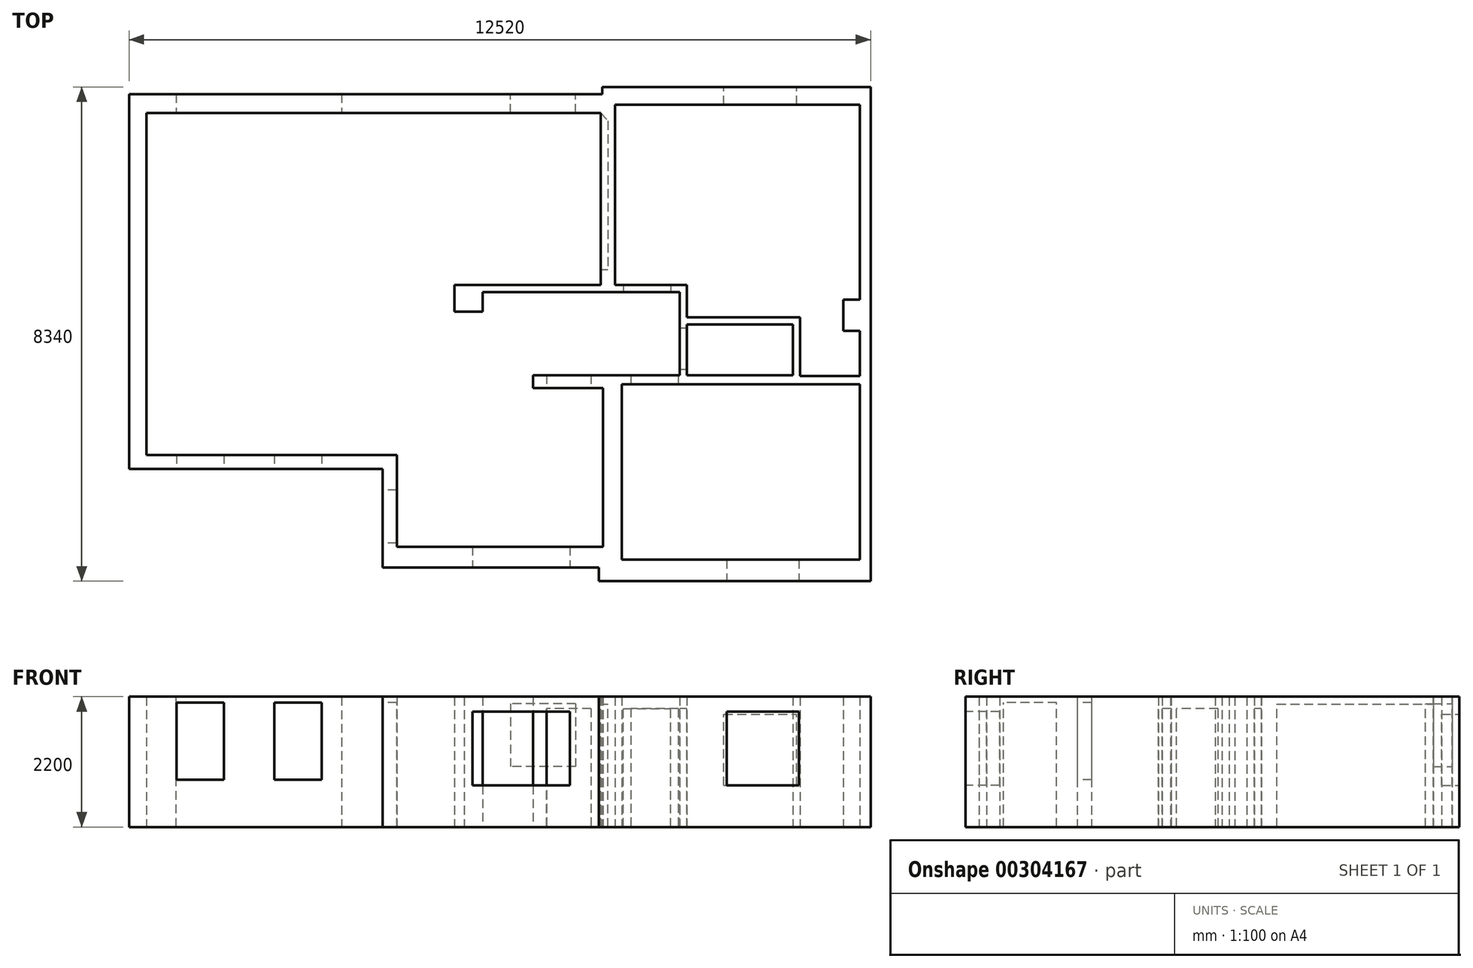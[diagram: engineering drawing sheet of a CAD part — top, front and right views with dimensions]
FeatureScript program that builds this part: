
annotation { "Feature Type Name" : "Feature", "Feature Type Description" : "" }
export const myFeature = defineFeature(function(context is Context, id is Id, definition is map)
    precondition{}
    {
        {
            var Q0;
            Q0=qCreatedBy(makeId("Top.planeOp"),FACE);
            var sketch = newSketch(context, id + "F0", { "sketchPlane" : qUnion([Q0])});
            skLineSegment(sketch, "E0", {"start": v(890, -1585.96) * mm, "end": v(-3390, -1585.96) * mm});
            skLineSegment(sketch, "E1", {"start": v(-3390, 4744.04) * mm, "end": v(-3390, -1585.96) * mm});
            skLineSegment(sketch, "E2", {"start": v(890, -3245.96) * mm, "end": v(4540, -3245.96) * mm});
            skLineSegment(sketch, "E3", {"start": v(4610, -2895.96) * mm, "end": v(1130, -2895.96) * mm});
            skLineSegment(sketch, "E4", {"start": v(4540, -3245.96) * mm, "end": v(4540, -3475.96) * mm});
            skLineSegment(sketch, "E5", {"start": v(4540, -3475.96) * mm, "end": v(9130, -3475.96) * mm});
            skLineSegment(sketch, "E6", {"start": v(9130, -3475.96) * mm, "end": v(9130, 4864.04) * mm});
            skLineSegment(sketch, "E7", {"start": v(9130, 4864.04) * mm, "end": v(4600, 4864.04) * mm});
            skLineSegment(sketch, "E8", {"start": v(4815, 4564.04) * mm, "end": v(8950, 4564.04) * mm});
            skLineSegment(sketch, "E9", {"start": v(8950, -3115.96) * mm, "end": v(4930, -3115.96) * mm});
            skLineSegment(sketch, "E10", {"start": v(8950, -155.96) * mm, "end": v(4930, -155.96) * mm});
            skLineSegment(sketch, "E11.bottom", {"start": v(8950, 1274.04) * mm, "end": v(8670, 1274.04) * mm});
            skLineSegment(sketch, "E11.top", {"start": v(8950, 744.04) * mm, "end": v(8670, 744.04) * mm});
            skLineSegment(sketch, "E11.right", {"start": v(8670, 1274.04) * mm, "end": v(8670, 744.04) * mm});
            skLineSegment(sketch, "E12", {"start": v(2020, 4424.04) * mm, "end": v(2020, 1518.96) * mm});
            skLineSegment(sketch, "E13", {"start": v(2020, 1518.96) * mm, "end": v(1110, 1518.96) * mm});
            skLineSegment(sketch, "E14", {"start": v(5905, 1400) * mm, "end": v(5905, 0) * mm});
            skLineSegment(sketch, "E15", {"start": v(7935, -15.96) * mm, "end": v(7935, 974.04) * mm});
            skLineSegment(sketch, "E16", {"start": v(7935, 974.04) * mm, "end": v(6025, 974.04) * mm});
            skLineSegment(sketch, "E17", {"start": v(6025, 974.04) * mm, "end": v(6025, 1524.04) * mm});
            skLineSegment(sketch, "E18", {"start": v(6025, 1524.04) * mm, "end": v(4815, 1524.04) * mm});
            skLineSegment(sketch, "E19", {"start": v(4815, 1524.04) * mm, "end": v(4815, 4564.04) * mm});
            skLineSegment(sketch, "E20", {"start": v(4695, 1524.04) * mm, "end": v(2215, 1524.04) * mm});
            skLineSegment(sketch, "E21", {"start": v(2215, 1524.04) * mm, "end": v(2215, 4424.04) * mm});
            skLineSegment(sketch, "E22", {"start": v(2100, 1400) * mm, "end": v(2100, 1070) * mm});
            skLineSegment(sketch, "E23", {"start": v(2100, 1070) * mm, "end": v(2580, 1070) * mm});
            skLineSegment(sketch, "E24", {"start": v(2580, 1070) * mm, "end": v(2580, 1400) * mm});
            skLineSegment(sketch, "E25", {"start": v(4695, 4424.04) * mm, "end": v(4695, 1524.04) * mm});
            skLineSegment(sketch, "E26", {"start": v(4695, 4424.04) * mm, "end": v(2215, 4424.04) * mm});
            skLineSegment(sketch, "E27", {"start": v(2020, 4424.04) * mm, "end": v(-3100, 4424.04) * mm});
            skLineSegment(sketch, "E28", {"start": v(-3100, 4424.04) * mm, "end": v(-3100, -1345.96) * mm});
            skLineSegment(sketch, "E29", {"start": v(890, -1585.96) * mm, "end": v(890, -3245.96) * mm});
            skLineSegment(sketch, "E30", {"start": v(4610, -215.96) * mm, "end": v(4610, -2895.96) * mm});
            skLineSegment(sketch, "E31", {"start": v(4930, -155.96) * mm, "end": v(4930, -3115.96) * mm});
            skLineSegment(sketch, "E32", {"start": v(8950, -155.96) * mm, "end": v(8950, -3115.96) * mm});
            skLineSegment(sketch, "E33", {"start": v(8950, -15.96) * mm, "end": v(8950, 744.04) * mm});
            skLineSegment(sketch, "E34", {"start": v(8950, 1274.04) * mm, "end": v(8950, 4564.04) * mm});
            skLineSegment(sketch, "E35", {"start": v(7935, -15.96) * mm, "end": v(8950, -15.96) * mm});
            skLineSegment(sketch, "E36", {"start": v(1110, 1400) * mm, "end": v(2100, 1400) * mm});
            skLineSegment(sketch, "E37", {"start": v(2580, 1400) * mm, "end": v(5905, 1400) * mm});
            skLineSegment(sketch, "E38", {"start": v(4610, -215.96) * mm, "end": v(3430, -215.96) * mm});
            skLineSegment(sketch, "E39", {"start": v(1130, -1345.96) * mm, "end": v(1130, -2895.96) * mm});
            skLineSegment(sketch, "E40", {"start": v(4600, 4864.04) * mm, "end": v(4600, 4744.04) * mm});
            skLineSegment(sketch, "E41", {"start": v(4600, 4744.04) * mm, "end": v(-3390, 4744.04) * mm});
            skLineSegment(sketch, "E42", {"start": v(-3100, -1345.96) * mm, "end": v(1130, -1345.96) * mm});
            skLineSegment(sketch, "E43", {"start": v(1110, 1400) * mm, "end": v(1110, 1518.96) * mm});
            skLineSegment(sketch, "E44", {"start": v(3430, -215.96) * mm, "end": v(3430, 0) * mm});
            skLineSegment(sketch, "E45", {"start": v(3430, 0) * mm, "end": v(5905, 0) * mm});
            skLineSegment(sketch, "E46.bottom", {"start": v(7815, 854.04) * mm, "end": v(6025, 854.04) * mm});
            skLineSegment(sketch, "E46.top", {"start": v(7815, 0) * mm, "end": v(6025, 0) * mm});
            skLineSegment(sketch, "E46.left", {"start": v(7815, 854.04) * mm, "end": v(7815, 0) * mm});
            skLineSegment(sketch, "E46.right", {"start": v(6025, 854.04) * mm, "end": v(6025, 0) * mm});
            skSolve(sketch);
        }
        {
            var Q0;
            Q0=makeQuery(id+"F0.imprint","IMPRINT",FACE,{"disambiguationData":[TD([[makeQuery(id+"F0.imprint","IMPRINT",EDGE,{"derivedFrom":sQuery(id+"F0.wireOp",EDGE,"E0")}),-1.0]])]});
            extrude(context, id + "F1", {"entities" : qUnion([Q0]), "depth" : 2200 * mm, "offsetDistance" : 25 * mm});
        }
        {
            var Q0;
            Q0=makeQuery(id+"F1.opExtrude","SWEPT_FACE",FACE,{"disambiguationData":[OSD([sQuery(id+"F0.wireOp",EDGE,"E27")])]});
            var sketch = newSketch(context, id + "F2", { "sketchPlane" : qUnion([Q0])});
            skLineSegment(sketch, "E47", {"start": v(-2600, 0) * mm, "end": v(-2600, 2199) * mm});
            skLineSegment(sketch, "E48", {"start": v(-2600, 2199) * mm, "end": v(200, 2199) * mm});
            skLineSegment(sketch, "E49", {"start": v(200, 2199) * mm, "end": v(200, 0) * mm});
            skLineSegment(sketch, "E50", {"start": v(200, 0) * mm, "end": v(-2600, 0) * mm});
            skSolve(sketch);
        }
        {
            var Q0;
            Q0 = qSketchRegion(id + "F2", true);
            extrude(context, id + "F3", {"entities" : qUnion([Q0]), "operationType" : NewBodyOperationType.REMOVE, "oppositeDirection" : true, "depth" : 350 * mm});
        }
        {
            var Q0;
            Q0=makeQuery(id+"F1.opExtrude","SWEPT_FACE",FACE,{"disambiguationData":[OSD([sQuery(id+"F0.wireOp",EDGE,"E12")])]});
            var sketch = newSketch(context, id + "F4", { "sketchPlane" : qUnion([Q0])});
            skLineSegment(sketch, "E51", {"start": v(-4424.04, 0) * mm, "end": v(-4424.04, 2200) * mm});
            skLineSegment(sketch, "E52", {"start": v(-4424.04, 2200) * mm, "end": v(-1518.96, 2200) * mm});
            skLineSegment(sketch, "E53", {"start": v(-1518.96, 2200) * mm, "end": v(-1518.96, 0) * mm});
            skLineSegment(sketch, "E54", {"start": v(-1518.96, 0) * mm, "end": v(-4424.04, 0) * mm});
            skSolve(sketch);
        }
        {
            var Q0;
            Q0 = qSketchRegion(id + "F4", true);
            extrude(context, id + "F5", {"entities" : qUnion([Q0]), "operationType" : NewBodyOperationType.REMOVE, "oppositeDirection" : true, "depth" : 250 * mm});
        }
        {
            var Q0;
            Q0=makeQuery(id+"F1.opExtrude","SWEPT_FACE",FACE,{"disambiguationData":[OSD([sQuery(id+"F0.wireOp",EDGE,"E36")])]});
            var sketch = newSketch(context, id + "F6", { "sketchPlane" : qUnion([Q0])});
            skLineSegment(sketch, "E55.bottom", {"start": v(1110, 0) * mm, "end": v(2100, 0) * mm});
            skLineSegment(sketch, "E55.top", {"start": v(1110, 2200) * mm, "end": v(2100, 2200) * mm});
            skLineSegment(sketch, "E55.left", {"start": v(1110, 0) * mm, "end": v(1110, 2200) * mm});
            skLineSegment(sketch, "E55.right", {"start": v(2100, 0) * mm, "end": v(2100, 2200) * mm});
            skSolve(sketch);
        }
        {
            var Q0;
            Q0 = qSketchRegion(id + "F6", true);
            extrude(context, id + "F7", {"entities" : qUnion([Q0]), "operationType" : NewBodyOperationType.REMOVE, "oppositeDirection" : true, "depth" : 130 * mm});
        }
        {
            var Q0;
            Q0=makeQuery(id+"F1.opExtrude","SWEPT_FACE",FACE,{"disambiguationData":[OSD([sQuery(id+"F0.wireOp",EDGE,"E38")])]});
            var sketch = newSketch(context, id + "F8", { "sketchPlane" : qUnion([Q0])});
            skLineSegment(sketch, "E56.bottom", {"start": v(3660, 0) * mm, "end": v(4410, 0) * mm});
            skLineSegment(sketch, "E56.top", {"start": v(3660, 2000) * mm, "end": v(4410, 2000) * mm});
            skLineSegment(sketch, "E56.left", {"start": v(3660, 0) * mm, "end": v(3660, 2000) * mm});
            skLineSegment(sketch, "E56.right", {"start": v(4410, 0) * mm, "end": v(4410, 2000) * mm});
            skSolve(sketch);
        }
        {
            var Q0;
            Q0 = qSketchRegion(id + "F8", true);
            extrude(context, id + "F9", {"entities" : qUnion([Q0]), "operationType" : NewBodyOperationType.REMOVE, "oppositeDirection" : true, "depth" : 250 * mm});
        }
        {
            var Q0;
            Q0=makeQuery(id+"F1.opExtrude","SWEPT_FACE",FACE,{"disambiguationData":[OSD([sQuery(id+"F0.wireOp",EDGE,"E37")])]});
            var sketch = newSketch(context, id + "F10", { "sketchPlane" : qUnion([Q0])});
            skLineSegment(sketch, "E57.bottom", {"start": v(4955, 0) * mm, "end": v(5755, 0) * mm});
            skLineSegment(sketch, "E57.top", {"start": v(4955, 2000) * mm, "end": v(5755, 2000) * mm});
            skLineSegment(sketch, "E57.left", {"start": v(4955, 0) * mm, "end": v(4955, 2000) * mm});
            skLineSegment(sketch, "E57.right", {"start": v(5755, 0) * mm, "end": v(5755, 2000) * mm});
            skSolve(sketch);
        }
        {
            var Q0;
            Q0 = qSketchRegion(id + "F10", true);
            extrude(context, id + "F11", {"entities" : qUnion([Q0]), "operationType" : NewBodyOperationType.REMOVE, "oppositeDirection" : true, "depth" : 200 * mm});
        }
        {
            var Q0;
            Q0=makeQuery(id+"F1.opExtrude","SWEPT_FACE",FACE,{"disambiguationData":[OSD([sQuery(id+"F0.wireOp",EDGE,"E10")])]});
            var sketch = newSketch(context, id + "F12", { "sketchPlane" : qUnion([Q0])});
            skLineSegment(sketch, "E58.bottom", {"start": v(5080, 0) * mm, "end": v(5880, 0) * mm});
            skLineSegment(sketch, "E58.top", {"start": v(5080, 2000) * mm, "end": v(5880, 2000) * mm});
            skLineSegment(sketch, "E58.left", {"start": v(5080, 0) * mm, "end": v(5080, 2000) * mm});
            skLineSegment(sketch, "E58.right", {"start": v(5880, 0) * mm, "end": v(5880, 2000) * mm});
            skSolve(sketch);
        }
        {
            var Q0;
            Q0 = qSketchRegion(id + "F12", true);
            extrude(context, id + "F13", {"entities" : qUnion([Q0]), "operationType" : NewBodyOperationType.REMOVE, "oppositeDirection" : true, "depth" : 200 * mm});
        }
        {
            var Q0;
            Q0=makeQuery(id+"F1.opExtrude","SWEPT_FACE",FACE,{"disambiguationData":[OSD([sQuery(id+"F0.wireOp",EDGE,"E0")])]});
            var sketch = newSketch(context, id + "F14", { "sketchPlane" : qUnion([Q0])});
            skLineSegment(sketch, "E59.bottom", {"start": v(-2590, 2100) * mm, "end": v(-1790, 2100) * mm});
            skLineSegment(sketch, "E59.top", {"start": v(-2590, 800) * mm, "end": v(-1790, 800) * mm});
            skLineSegment(sketch, "E59.left", {"start": v(-2590, 2100) * mm, "end": v(-2590, 800) * mm});
            skLineSegment(sketch, "E59.right", {"start": v(-1790, 2100) * mm, "end": v(-1790, 800) * mm});
            skLineSegment(sketch, "E60.bottom", {"start": v(-940, 2100) * mm, "end": v(-140, 2100) * mm});
            skLineSegment(sketch, "E60.top", {"start": v(-940, 800) * mm, "end": v(-140, 800) * mm});
            skLineSegment(sketch, "E60.left", {"start": v(-940, 2100) * mm, "end": v(-940, 800) * mm});
            skLineSegment(sketch, "E60.right", {"start": v(-140, 2100) * mm, "end": v(-140, 800) * mm});
            skSolve(sketch);
        }
        {
            var Q0;
            Q0 = qSketchRegion(id + "F14", true);
            extrude(context, id + "F15", {"entities" : qUnion([Q0]), "operationType" : NewBodyOperationType.REMOVE, "endBound" : BoundingType.UP_TO_NEXT, "oppositeDirection" : true, "depth" : 350 * mm});
        }
        {
            var Q0;
            Q0=makeQuery(id+"F1.opExtrude","SWEPT_FACE",FACE,{"disambiguationData":[OSD([sQuery(id+"F0.wireOp",EDGE,"E2")])]});
            var sketch = newSketch(context, id + "F16", { "sketchPlane" : qUnion([Q0])});
            skLineSegment(sketch, "E61.bottom", {"start": v(2410, 1950) * mm, "end": v(4050, 1950) * mm});
            skLineSegment(sketch, "E61.top", {"start": v(2410, 700) * mm, "end": v(4050, 700) * mm});
            skLineSegment(sketch, "E61.left", {"start": v(2410, 1950) * mm, "end": v(2410, 700) * mm});
            skLineSegment(sketch, "E61.right", {"start": v(4050, 1950) * mm, "end": v(4050, 700) * mm});
            skSolve(sketch);
        }
        {
            var Q0;
            Q0 = qSketchRegion(id + "F16", true);
            extrude(context, id + "F17", {"entities" : qUnion([Q0]), "operationType" : NewBodyOperationType.REMOVE, "endBound" : BoundingType.UP_TO_NEXT, "oppositeDirection" : true, "depth" : 25 * mm});
        }
        {
            var Q0;
            Q0=makeQuery(id+"F1.opExtrude","SWEPT_FACE",FACE,{"disambiguationData":[OSD([sQuery(id+"F0.wireOp",EDGE,"E5")])]});
            var sketch = newSketch(context, id + "F18", { "sketchPlane" : qUnion([Q0])});
            skLineSegment(sketch, "E62.bottom", {"start": v(6700, 1950) * mm, "end": v(7920, 1950) * mm});
            skLineSegment(sketch, "E62.top", {"start": v(6700, 700) * mm, "end": v(7920, 700) * mm});
            skLineSegment(sketch, "E62.left", {"start": v(6700, 1950) * mm, "end": v(6700, 700) * mm});
            skLineSegment(sketch, "E62.right", {"start": v(7920, 1950) * mm, "end": v(7920, 700) * mm});
            skSolve(sketch);
        }
        {
            var Q0;
            Q0 = qSketchRegion(id + "F18", true);
            extrude(context, id + "F19", {"entities" : qUnion([Q0]), "operationType" : NewBodyOperationType.REMOVE, "endBound" : BoundingType.UP_TO_NEXT, "oppositeDirection" : true, "depth" : 25 * mm});
        }
        {
            var Q0;
            Q0=makeQuery(id+"F1.opExtrude","SWEPT_FACE",FACE,{"disambiguationData":[OSD([sQuery(id+"F0.wireOp",EDGE,"E7")])]});
            var sketch = newSketch(context, id + "F20", { "sketchPlane" : qUnion([Q0])});
            skLineSegment(sketch, "E63.bottom", {"start": v(-7880, 1900) * mm, "end": v(-6650, 1900) * mm});
            skLineSegment(sketch, "E63.top", {"start": v(-7880, 700) * mm, "end": v(-6650, 700) * mm});
            skLineSegment(sketch, "E63.left", {"start": v(-7880, 1900) * mm, "end": v(-7880, 700) * mm});
            skLineSegment(sketch, "E63.right", {"start": v(-6650, 1900) * mm, "end": v(-6650, 700) * mm});
            skSolve(sketch);
        }
        {
            var Q0;
            Q0 = qSketchRegion(id + "F20", true);
            extrude(context, id + "F21", {"entities" : qUnion([Q0]), "operationType" : NewBodyOperationType.REMOVE, "endBound" : BoundingType.UP_TO_NEXT, "oppositeDirection" : true, "depth" : 25 * mm});
        }
        {
            var Q0;
            Q0=makeQuery(id+"F1.opExtrude","SWEPT_FACE",FACE,{"disambiguationData":[OSD([sQuery(id+"F0.wireOp",EDGE,"E41")])]});
            var sketch = newSketch(context, id + "F22", { "sketchPlane" : qUnion([Q0])});
            skLineSegment(sketch, "E64.bottom", {"start": v(-4150, 2080) * mm, "end": v(-3050, 2080) * mm});
            skLineSegment(sketch, "E64.top", {"start": v(-4150, 1020) * mm, "end": v(-3050, 1020) * mm});
            skLineSegment(sketch, "E64.left", {"start": v(-4150, 2080) * mm, "end": v(-4150, 1020) * mm});
            skLineSegment(sketch, "E64.right", {"start": v(-3050, 2080) * mm, "end": v(-3050, 1020) * mm});
            skSolve(sketch);
        }
        {
            var Q0;
            Q0 = qSketchRegion(id + "F22", true);
            extrude(context, id + "F23", {"entities" : qUnion([Q0]), "operationType" : NewBodyOperationType.REMOVE, "endBound" : BoundingType.UP_TO_NEXT, "oppositeDirection" : true, "depth" : 25 * mm});
        }
        {
            var Q0;
            Q0=makeQuery(id+"F1.opExtrude","SWEPT_FACE",FACE,{"disambiguationData":[OSD([sQuery(id+"F0.wireOp",EDGE,"E29")])]});
            var sketch = newSketch(context, id + "F24", { "sketchPlane" : qUnion([Q0])});
            skLineSegment(sketch, "E65.bottom", {"start": v(1935.96, 0) * mm, "end": v(2835.96, 0) * mm});
            skLineSegment(sketch, "E65.top", {"start": v(1935.96, 2100) * mm, "end": v(2835.96, 2100) * mm});
            skLineSegment(sketch, "E65.left", {"start": v(1935.96, 0) * mm, "end": v(1935.96, 2100) * mm});
            skLineSegment(sketch, "E65.right", {"start": v(2835.96, 0) * mm, "end": v(2835.96, 2100) * mm});
            skSolve(sketch);
        }
        {
            var Q0;
            Q0 = qSketchRegion(id + "F24", true);
            extrude(context, id + "F25", {"entities" : qUnion([Q0]), "operationType" : NewBodyOperationType.REMOVE, "endBound" : BoundingType.UP_TO_NEXT, "oppositeDirection" : true, "depth" : 25 * mm});
        }
        {
            var Q0;
            Q0=makeQuery(id+"F1.opExtrude","SWEPT_FACE",FACE,{"disambiguationData":[OSD([sQuery(id+"F0.wireOp",EDGE,"E14")])]});
            var sketch = newSketch(context, id + "F26", { "sketchPlane" : qUnion([Q0])});
            skLineSegment(sketch, "E66.bottom", {"start": v(-790, 0) * mm, "end": v(-90, 0) * mm});
            skLineSegment(sketch, "E66.top", {"start": v(-790, 2000) * mm, "end": v(-90, 2000) * mm});
            skLineSegment(sketch, "E66.left", {"start": v(-790, 0) * mm, "end": v(-790, 2000) * mm});
            skLineSegment(sketch, "E66.right", {"start": v(-90, 0) * mm, "end": v(-90, 2000) * mm});
            skSolve(sketch);
        }
        {
            var Q0;
            Q0 = qSketchRegion(id + "F26", true);
            extrude(context, id + "F27", {"entities" : qUnion([Q0]), "operationType" : NewBodyOperationType.REMOVE, "endBound" : BoundingType.UP_TO_NEXT, "oppositeDirection" : true, "depth" : 25 * mm});
        }
        {
            var Q0;
            Q0=makeQuery(id+"F1.opExtrude","SWEPT_FACE",FACE,{"disambiguationData":[OSD([sQuery(id+"F0.wireOp",EDGE,"E25")])]});
            var sketch = newSketch(context, id + "F28", { "sketchPlane" : qUnion([Q0])});
            skLineSegment(sketch, "E67", {"start": v(-1784.04, 0) * mm, "end": v(-1784.04, 2075) * mm});
            skLineSegment(sketch, "E68", {"start": v(-1784.04, 2075) * mm, "end": v(-4424.04, 2075) * mm});
            skLineSegment(sketch, "E69", {"start": v(-4424.04, 2075) * mm, "end": v(-4424.04, 2200) * mm});
            skLineSegment(sketch, "E70", {"start": v(-4424.04, 2200) * mm, "end": v(-1524.04, 2200) * mm});
            skLineSegment(sketch, "E71", {"start": v(-1524.04, 2200) * mm, "end": v(-1524.04, 0) * mm});
            skLineSegment(sketch, "E72", {"start": v(-1524.04, 0) * mm, "end": v(-1784.04, 0) * mm});
            skSolve(sketch);
        }
        {
            var Q0;
            Q0=makeQuery(id+"F28.imprint","IMPRINT",FACE,{"disambiguationData":[TD([[makeQuery(id+"F28.imprint","IMPRINT",EDGE,{"derivedFrom":sQuery(id+"F28.wireOp",EDGE,"E67")}),-1.0]])]});
            extrude(context, id + "F29", {"entities" : qUnion([Q0]), "operationType" : NewBodyOperationType.ADD, "depth" : 125 * mm, "offsetDistance" : 25 * mm});
        }
        {
            var Q0;
            Q0=makeQuery(id+"F29.opExtrude","SWEPT_FACE",FACE,{"disambiguationData":[OSD([sQuery(id+"F28.wireOp",EDGE,"E68")])]});
            var sketch = newSketch(context, id + "F30", { "sketchPlane" : qUnion([Q0])});
            skLineSegment(sketch, "E73", {"start": v(4570, -4424.04) * mm, "end": v(4695, -4288.74) * mm});
            skLineSegment(sketch, "E74", {"start": v(4695, -4288.74) * mm, "end": v(4695, -4424.04) * mm});
            skLineSegment(sketch, "E75", {"start": v(4695, -4424.04) * mm, "end": v(4570, -4424.04) * mm});
            skSolve(sketch);
        }
        {
            var Q0;
            Q0=makeQuery(id+"F30.imprint","IMPRINT",FACE,{"disambiguationData":[TD([[makeQuery(id+"F30.imprint","IMPRINT",EDGE,{"derivedFrom":sQuery(id+"F30.wireOp",EDGE,"E73")}),-1.0]])]});
            extrude(context, id + "F31", {"entities" : qUnion([Q0]), "operationType" : NewBodyOperationType.ADD, "depth" : 2075 * mm, "offsetDistance" : 25 * mm});
        }
    });
